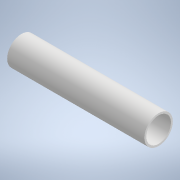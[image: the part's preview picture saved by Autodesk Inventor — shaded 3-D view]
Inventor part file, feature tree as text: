
AUTODESK INVENTOR PART (.ipt)
format: ipt  version: 2022 (Build 260153000, 153)  size: 97,280 bytes
history: native  units: mm
features: other x1, extrude x1, sketch x1
ambient origin geometry x8: Origin, YZ Plane, XZ Plane, XY Plane, X Axis, Y Axis, Z Axis, Center Point
bodies: Body1 (feature_tree)
feature tree (3):
  other  "Твердое тело1"
  extrude  "Выдавливание1"  Depth=24.9mm
  sketch  "Эскиз1"
